FCSTD DOCUMENT  (FreeCAD 0.19R)
Label: test_ifc_points
License: All rights reserved
LicenseURL: http://en.wikipedia.org/wiki/All_rights_reserved
objects: Part::FeaturePython×8
note: 8 computed .brp shape members not serialized (recipe doc carries the construction recipe); baked Part::Feature solids carry a one-line shape summary decoded from their .brp

FEATURE [Part::FeaturePython] Point  # WARN: FeaturePython — macro-defined, semantics opaque (R4)
  X = 0
  Y = 0
  Z = 0
FEATURE [Part::FeaturePython] Point001  # WARN: FeaturePython — macro-defined, semantics opaque (R4)
  Placement = pos=(1000,0,0) rot=(0,0,1;0rad)
  X = 1000
  Y = 0
  Z = 0
FEATURE [Part::FeaturePython] Point002  # WARN: FeaturePython — macro-defined, semantics opaque (R4)
  Placement = pos=(0,1000,0) rot=(0,0,1;0rad)
  X = 0
  Y = 1000
  Z = 0
FEATURE [Part::FeaturePython] Point003  # WARN: FeaturePython — macro-defined, semantics opaque (R4)
  Placement = pos=(1000,1000,0) rot=(0,0,1;0rad)
  X = 1000
  Y = 1000
  Z = 0
FEATURE [Part::FeaturePython] Component  label="IFCPoint1"  # Arch/BIM 143 (typed FeaturePython)
  Base = -> Point
  Description = test
  HorizontalArea = 0
  IfcData = attributes={"GlobalId": {"name": "GlobalId", "type": "IfcGloballyUniqueId", "is_enum": false, "enum_values": []}, "Description": {"... (+1008 chars omitted),+1 more (map truncated)
  IfcType = 143
  MoveBase = false
  MoveWithHost = false
  PerimeterLength = 0
  VerticalArea = 0
FEATURE [Part::FeaturePython] Component001  label="IFCPoint2"  # Arch/BIM 143 (typed FeaturePython)
  Base = -> Point003
  HorizontalArea = 0
  IfcData = attributes={"GlobalId": {"name": "GlobalId", "type": "IfcGloballyUniqueId", "is_enum": false, "enum_values": []}, "Description": {"... (+538 chars omitted),+1 more (map truncated)
  IfcType = 143
  MoveBase = false
  MoveWithHost = false
  PerimeterLength = 0
  Placement = pos=(1000,1000,0) rot=(0,0,1;0rad)
  VerticalArea = 0
FEATURE [Part::FeaturePython] Component002  label="IFCPoint3"  # Arch/BIM 143 (typed FeaturePython)
  Base = -> Point002
  HorizontalArea = 0
  IfcData = attributes={"GlobalId": {"name": "GlobalId", "type": "IfcGloballyUniqueId", "is_enum": false, "enum_values": []}, "Description": {"... (+538 chars omitted),+1 more (map truncated)
  IfcType = 143
  MoveBase = false
  MoveWithHost = false
  PerimeterLength = 0
  Placement = pos=(0,1000,0) rot=(0,0,1;0rad)
  VerticalArea = 0
FEATURE [Part::FeaturePython] Component003  label="IFCPoint4"  # Arch/BIM 143 (typed FeaturePython)
  Base = -> Point001
  HorizontalArea = 0
  IfcData = attributes={"GlobalId": {"name": "GlobalId", "type": "IfcGloballyUniqueId", "is_enum": false, "enum_values": []}, "Description": {"... (+538 chars omitted),+1 more (map truncated)
  IfcType = 143
  MoveBase = false
  MoveWithHost = false
  PerimeterLength = 0
  Placement = pos=(1000,0,0) rot=(0,0,1;0rad)
  VerticalArea = 0
